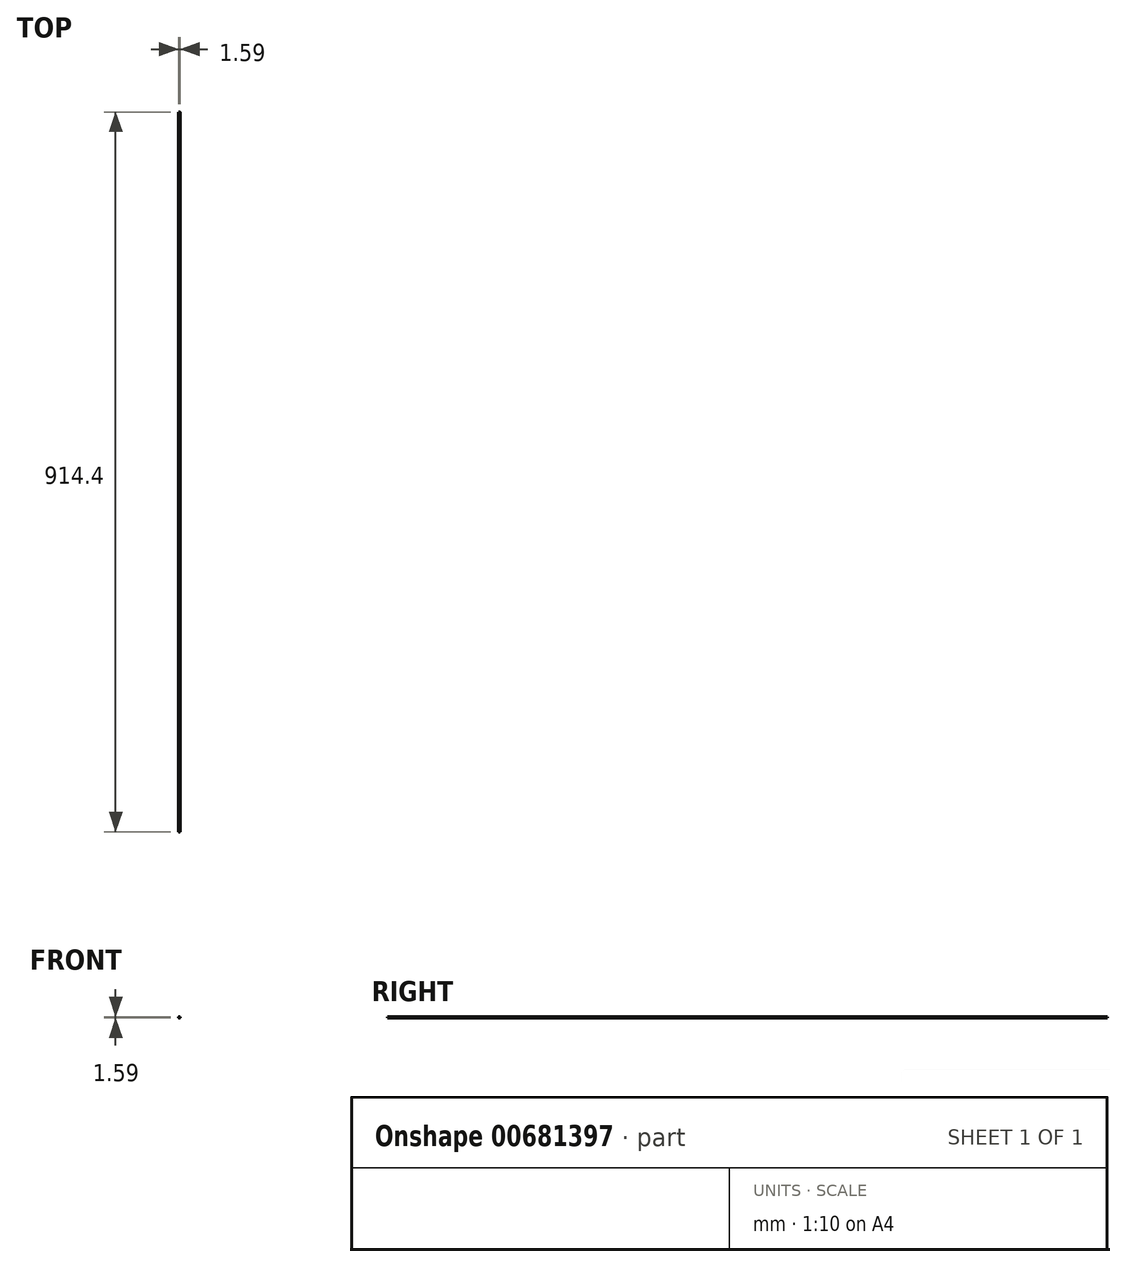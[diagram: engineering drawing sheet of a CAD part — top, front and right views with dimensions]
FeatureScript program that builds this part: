
annotation { "Feature Type Name" : "Feature", "Feature Type Description" : "" }
export const myFeature = defineFeature(function(context is Context, id is Id, definition is map)
    precondition{}
    {
        {
            var Q0;
            Q0=qCreatedBy(makeId("Front.planeOp"),FACE);
            var sketch = newSketch(context, id + "F0", { "sketchPlane" : qUnion([Q0])});
            skCircle(sketch, "E0", {"center": v(27.54, 28.28) * mm, "radius": 0.8 * mm});
            skSolve(sketch);
        }
        {
            var Q0;
            Q0=makeQuery(id+"F0.imprint","IMPRINT",FACE,{"disambiguationData":[TD([[makeQuery(id+"F0.imprint","IMPRINT",EDGE,{"derivedFrom":sQuery(id+"F0.wireOp",EDGE,"E0")}),1.0]])]});
            extrude(context, id + "F1", {"entities" : qUnion([Q0]), "depth" : 914.4 * mm, "offsetDistance" : 25.4 * mm});
        }
    });
